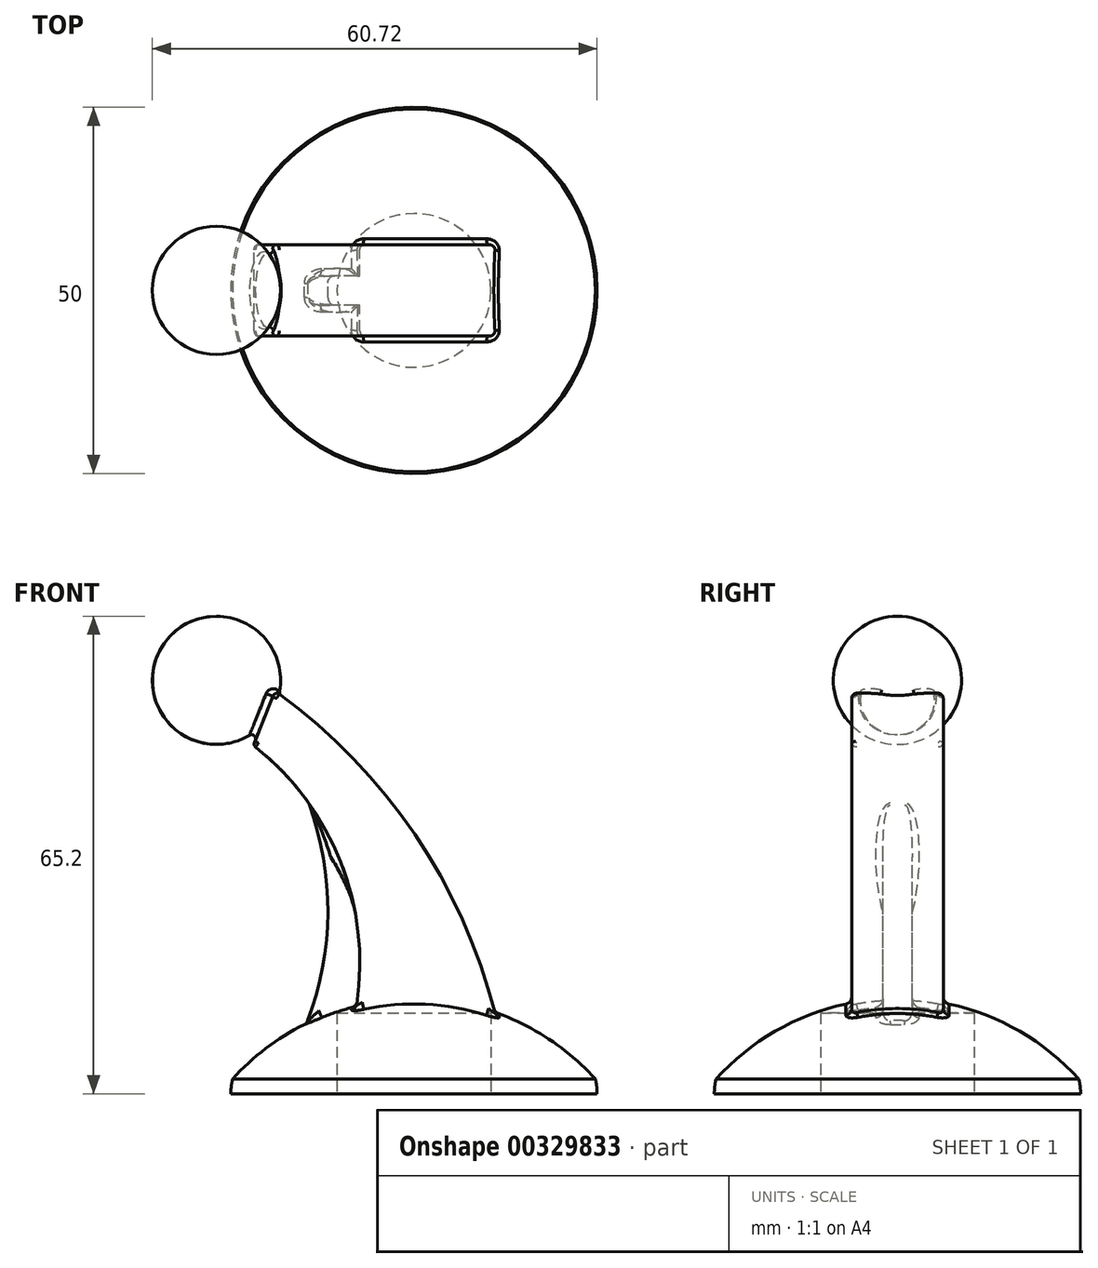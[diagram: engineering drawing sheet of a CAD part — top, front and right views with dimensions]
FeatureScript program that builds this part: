
annotation { "Feature Type Name" : "Feature", "Feature Type Description" : "" }
export const myFeature = defineFeature(function(context is Context, id is Id, definition is map)
    precondition{}
    {
        {
            assignVariable(context, id + "F0", {"name" : "magDepth", "anyValue" : 11});
        }
        {
            var Q0;
            Q0=qCreatedBy(makeId("Front.planeOp"),FACE);
            var sketch = newSketch(context, id + "F1", { "sketchPlane" : qUnion([Q0])});
            skLineSegment(sketch, "E0", {"start": v(0, 13) * mm, "end": v(0, 0) * mm});
            skLineSegment(sketch, "E1", {"start": v(0, 0) * mm, "end": v(25, 0) * mm});
            skArc(sketch, "E2", {"start": v(25, 0) * mm, "mid": v(24.94, 1) * mm, "end": v(24.77, 2) * mm});
            skArc(sketch, "E3", {"start": v(24.77, 2) * mm, "mid": v(13.55, 10.13) * mm, "end": v(0, 13) * mm});
            skLineSegment(sketch, "E4", {"start": v(0, 13) * mm, "end": v(-1.98, 13) * mm, "construction": true});
            skLineSegment(sketch, "E5", {"start": v(25, 0) * mm, "end": v(25, -2.25) * mm, "construction": true});
            skSolve(sketch);
        }
        {
            var Q0;
            Q0=makeQuery(id+"F1.imprint","IMPRINT",FACE,{"disambiguationData":[TD([[makeQuery(id+"F1.imprint","IMPRINT",EDGE,{"derivedFrom":sQuery(id+"F1.wireOp",EDGE,"E0")}),1.0]])]});
            var Q1;
            Q1=sQuery(id+"F1.wireOp",EDGE,"E0");
            revolve(context, id + "F2", {"entities" : qUnion([Q0]), "axis" : qUnion([Q1]), "revolveType" : RevolveType.FULL});
        }
        {
            var Q0;
            Q0=qCreatedBy(makeId("Front.planeOp"),FACE);
            var sketch = newSketch(context, id + "F3", { "sketchPlane" : qUnion([Q0])});
            skArc(sketch, "E6", {"start": v(13.03, 0) * mm, "mid": v(2.93, 30.93) * mm, "end": v(-18.97, 55) * mm});
            skArc(sketch, "E7", {"start": v(-11.84, 0) * mm, "mid": v(-8.2, 25.63) * mm, "end": v(-21.94, 47.57) * mm});
            skLineSegment(sketch, "E8", {"start": v(-21.94, 47.57) * mm, "end": v(-18.97, 55) * mm});
            skLineSegment(sketch, "E9", {"start": v(-11.84, 0) * mm, "end": v(13.03, 0) * mm});
            skSolve(sketch);
        }
        {
            var Q0;
            Q0 = qSketchRegion(id + "F3", true);
            extrude(context, id + "F4", {"entities" : qUnion([Q0]), "operationType" : NewBodyOperationType.ADD, "depth" : 12.5 * mm, "offsetDistance" : 25 * mm, "symmetric" : true});
        }
        {
            var Q0;
            Q0=qCreatedBy(makeId("Front.planeOp"),FACE);
            var sketch = newSketch(context, id + "F5", { "sketchPlane" : qUnion([Q0])});
            skArc(sketch, "E10", {"start": v(-7.92, 11.44) * mm, "mid": v(-8.33, 26.17) * mm, "end": v(-14.34, 39.62) * mm});
            skArc(sketch, "E11", {"start": v(-17.04, 4.49) * mm, "mid": v(-11.88, 21.76) * mm, "end": v(-14.34, 39.62) * mm});
            skLineSegment(sketch, "E12", {"start": v(-17.04, 4.49) * mm, "end": v(-7.92, 11.44) * mm});
            skSolve(sketch);
        }
        {
            var Q0;
            Q0 = qSketchRegion(id + "F5", true);
            extrude(context, id + "F6", {"entities" : qUnion([Q0]), "operationType" : NewBodyOperationType.ADD, "depth" : 4 * mm, "offsetDistance" : 25 * mm, "symmetric" : true});
        }
        {
            var Q0;
            Q0=qCreatedBy(makeId("Front.planeOp"),FACE);
            var sketch = newSketch(context, id + "F7", { "sketchPlane" : qUnion([Q0])});
            skArc(sketch, "E13", {"start": v(-26.97, 65.2) * mm, "mid": v(-35.72, 56.45) * mm, "end": v(-26.97, 47.7) * mm});
            skLineSegment(sketch, "E14", {"start": v(-26.97, 65.2) * mm, "end": v(-26.97, 47.7) * mm});
            skSolve(sketch);
        }
        {
            var Q0;
            Q0=makeQuery(id+"F7.imprint","IMPRINT",FACE,{"disambiguationData":[TD([[makeQuery(id+"F7.imprint","IMPRINT",EDGE,{"derivedFrom":sQuery(id+"F7.wireOp",EDGE,"E13")}),1.0]])]});
            var Q1;
            Q1=sQuery(id+"F7.wireOp",EDGE,"E14");
            revolve(context, id + "F8", {"operationType" : NewBodyOperationType.ADD, "entities" : qUnion([Q0]), "axis" : qUnion([Q1]), "revolveType" : RevolveType.FULL});
        }
        {
            var Q0;
            Q0=makeQuery(id+"F4.opExtrude","CAP_EDGE",EDGE,{"disambiguationData":[OSD([sQuery(id+"F3.wireOp",EDGE,"E8")])],"isStart":true});
            var Q1;
            Q1=makeQuery(id+"F4.opExtrude","CAP_EDGE",EDGE,{"disambiguationData":[OSD([sQuery(id+"F3.wireOp",EDGE,"E8")])],"isStart":false});
            var Q2;
            {var subQ0=sQuery(id+"F3.wireOp",EDGE,"E8");var subQ1=sQuery(id+"F3.wireOp",EDGE,"E7");Q2=makeQuery(id+"F8.boolean.opBoolean","SPLIT",EDGE,{"disambiguationData":[TD([makeQuery(id+"F4.opExtrude","CAP_FACE",FACE,{"disambiguationData":[OSD([sQuery(id+"F3.wireOp",EDGE,"E6"),subQ1,subQ0,sQuery(id+"F3.wireOp",EDGE,"E9")])],"isStart":false})])],"derivedFrom":makeQuery(id+"F4.opExtrude","SWEPT_EDGE",EDGE,{"disambiguationData":[OSD([subQ1,subQ0])]})});}
            var Q3;
            {var subQ0=sQuery(id+"F3.wireOp",EDGE,"E8");var subQ1=sQuery(id+"F3.wireOp",EDGE,"E7");Q3=makeQuery(id+"F8.boolean.opBoolean","SPLIT",EDGE,{"disambiguationData":[TD([makeQuery(id+"F4.opExtrude","CAP_FACE",FACE,{"disambiguationData":[OSD([sQuery(id+"F3.wireOp",EDGE,"E6"),subQ1,subQ0,sQuery(id+"F3.wireOp",EDGE,"E9")])],"isStart":true})])],"derivedFrom":makeQuery(id+"F4.opExtrude","SWEPT_EDGE",EDGE,{"disambiguationData":[OSD([subQ1,subQ0])]})});}
            var Q4;
            {var subQ0=sQuery(id+"F3.wireOp",EDGE,"E6");var subQ1=sQuery(id+"F3.wireOp",EDGE,"E8");Q4=makeQuery(id+"F8.boolean.opBoolean","SPLIT",EDGE,{"disambiguationData":[TD([makeQuery(id+"F4.opExtrude","CAP_FACE",FACE,{"disambiguationData":[OSD([subQ0,sQuery(id+"F3.wireOp",EDGE,"E7"),subQ1,sQuery(id+"F3.wireOp",EDGE,"E9")])],"isStart":false})])],"derivedFrom":makeQuery(id+"F4.opExtrude","SWEPT_EDGE",EDGE,{"disambiguationData":[OSD([subQ0,subQ1])]})});}
            var Q5;
            {var subQ0=sQuery(id+"F3.wireOp",EDGE,"E6");var subQ1=sQuery(id+"F3.wireOp",EDGE,"E8");Q5=makeQuery(id+"F8.boolean.opBoolean","SPLIT",EDGE,{"disambiguationData":[TD([makeQuery(id+"F4.opExtrude","CAP_FACE",FACE,{"disambiguationData":[OSD([subQ0,sQuery(id+"F3.wireOp",EDGE,"E7"),subQ1,sQuery(id+"F3.wireOp",EDGE,"E9")])],"isStart":true})])],"derivedFrom":makeQuery(id+"F4.opExtrude","SWEPT_EDGE",EDGE,{"disambiguationData":[OSD([subQ0,subQ1])]})});}
            var Q6;
            Q6=makeQuery(id+"F8.boolean.opBoolean","INTERSECT",EDGE,{"derivedFrom":[makeQuery(id+"F4.opExtrude","SWEPT_FACE",FACE,{"disambiguationData":[OSD([sQuery(id+"F3.wireOp",EDGE,"E6")])]}),makeQuery(id+"F8.opRevolve","SWEPT_FACE",FACE,{"disambiguationData":[OSD([sQuery(id+"F7.wireOp",EDGE,"E13")])]})]});
            var Q7;
            Q7=makeQuery(id+"F8.boolean.opBoolean","INTERSECT",EDGE,{"derivedFrom":[makeQuery(id+"F4.opExtrude","SWEPT_FACE",FACE,{"disambiguationData":[OSD([sQuery(id+"F3.wireOp",EDGE,"E7")])]}),makeQuery(id+"F8.opRevolve","SWEPT_FACE",FACE,{"disambiguationData":[OSD([sQuery(id+"F7.wireOp",EDGE,"E13")])]})]});
            var Q8;
            Q8=makeQuery(id+"F8.boolean.opBoolean","INTERSECT",EDGE,{"disambiguationData":[OD(0.0)],"derivedFrom":[makeQuery(id+"F4.opExtrude","SWEPT_FACE",FACE,{"disambiguationData":[OSD([sQuery(id+"F3.wireOp",EDGE,"E8")])]}),makeQuery(id+"F8.opRevolve","SWEPT_FACE",FACE,{"disambiguationData":[OSD([sQuery(id+"F7.wireOp",EDGE,"E13")])]})]});
            fillet(context, id + "F9", {"entities" : qUnion([Q0, Q1, Q2, Q3, Q4, Q5, Q6, Q7, Q8]), "radius" : .55 * mm, "tangentPropagation" : true, "allowEdgeOverflow" : false});
        }
        {
            var Q0;
            Q0=makeQuery(id+"F4.opExtrude","CAP_EDGE",EDGE,{"disambiguationData":[OSD([sQuery(id+"F3.wireOp",EDGE,"E7")])],"isStart":false});
            var Q1;
            Q1=makeQuery(id+"F4.opExtrude","CAP_EDGE",EDGE,{"disambiguationData":[OSD([sQuery(id+"F3.wireOp",EDGE,"E6")])],"isStart":false});
            var Q2;
            Q2=makeQuery(id+"F4.opExtrude","CAP_EDGE",EDGE,{"disambiguationData":[OSD([sQuery(id+"F3.wireOp",EDGE,"E7")])],"isStart":true});
            var Q3;
            Q3=makeQuery(id+"F4.opExtrude","CAP_EDGE",EDGE,{"disambiguationData":[OSD([sQuery(id+"F3.wireOp",EDGE,"E6")])],"isStart":true});
            fillet(context, id + "F10", {"entities" : qUnion([Q0, Q1, Q2, Q3]), "radius" : .7 * mm, "tangentPropagation" : true, "allowEdgeOverflow" : false});
        }
        {
            var Q0;
            Q0=makeQuery(id+"F6.opExtrude","CAP_EDGE",EDGE,{"disambiguationData":[OSD([sQuery(id+"F5.wireOp",EDGE,"E11")])],"isStart":false});
            var Q1;
            Q1=makeQuery(id+"F6.opExtrude","SWEPT_FACE",FACE,{"disambiguationData":[OSD([sQuery(id+"F5.wireOp",EDGE,"E11")])]});
            var Q2;
            Q2=makeQuery(id+"F6.boolean.opBoolean","INTERSECT",EDGE,{"derivedFrom":[makeQuery(id+"F2.opRevolve","SWEPT_FACE",FACE,{"disambiguationData":[OSD([sQuery(id+"F1.wireOp",EDGE,"E3")])]}),makeQuery(id+"F6.opExtrude","SWEPT_FACE",FACE,{"disambiguationData":[OSD([sQuery(id+"F5.wireOp",EDGE,"E11")])]})]});
            var Q3;
            Q3=makeQuery(id+"F4.boolean.opBoolean","INTERSECT",EDGE,{"derivedFrom":[makeQuery(id+"F2.opRevolve","SWEPT_FACE",FACE,{"disambiguationData":[OSD([sQuery(id+"F1.wireOp",EDGE,"E3")])]}),makeQuery(id+"F4.opExtrude","CAP_FACE",FACE,{"disambiguationData":[OSD([sQuery(id+"F3.wireOp",EDGE,"E6"),sQuery(id+"F3.wireOp",EDGE,"E7"),sQuery(id+"F3.wireOp",EDGE,"E8"),sQuery(id+"F3.wireOp",EDGE,"E9")])],"isStart":false})]});
            var Q4;
            Q4=makeQuery(id+"F10.opFillet","BLEND_EDGE",EDGE,{"blendedFrom":[makeQuery(id+"F4.opExtrude","CAP_EDGE",EDGE,{"disambiguationData":[OSD([sQuery(id+"F3.wireOp",EDGE,"E7")])],"isStart":false}),makeQuery(id+"F2.opRevolve","SWEPT_FACE",FACE,{"disambiguationData":[OSD([sQuery(id+"F1.wireOp",EDGE,"E3")])]})],"blendedInto":[makeQuery(id+"F2.opRevolve","SWEPT_FACE",FACE,{"disambiguationData":[OSD([sQuery(id+"F1.wireOp",EDGE,"E3")])]})]});
            var Q5;
            Q5=makeQuery(id+"F10.opFillet","BLEND_EDGE",EDGE,{"blendedFrom":[makeQuery(id+"F4.opExtrude","CAP_EDGE",EDGE,{"disambiguationData":[OSD([sQuery(id+"F3.wireOp",EDGE,"E6")])],"isStart":false}),makeQuery(id+"F2.opRevolve","SWEPT_FACE",FACE,{"disambiguationData":[OSD([sQuery(id+"F1.wireOp",EDGE,"E3")])]})],"blendedInto":[makeQuery(id+"F2.opRevolve","SWEPT_FACE",FACE,{"disambiguationData":[OSD([sQuery(id+"F1.wireOp",EDGE,"E3")])]})]});
            var Q6;
            Q6=makeQuery(id+"F4.boolean.opBoolean","INTERSECT",EDGE,{"derivedFrom":[makeQuery(id+"F2.opRevolve","SWEPT_FACE",FACE,{"disambiguationData":[OSD([sQuery(id+"F1.wireOp",EDGE,"E3")])]}),makeQuery(id+"F4.opExtrude","SWEPT_FACE",FACE,{"disambiguationData":[OSD([sQuery(id+"F3.wireOp",EDGE,"E6")])]})]});
            var Q7;
            Q7=makeQuery(id+"F10.opFillet","BLEND_EDGE",EDGE,{"blendedFrom":[makeQuery(id+"F4.opExtrude","CAP_EDGE",EDGE,{"disambiguationData":[OSD([sQuery(id+"F3.wireOp",EDGE,"E6")])],"isStart":true}),makeQuery(id+"F2.opRevolve","SWEPT_FACE",FACE,{"disambiguationData":[OSD([sQuery(id+"F1.wireOp",EDGE,"E3")])]})],"blendedInto":[makeQuery(id+"F2.opRevolve","SWEPT_FACE",FACE,{"disambiguationData":[OSD([sQuery(id+"F1.wireOp",EDGE,"E3")])]})]});
            var Q8;
            Q8=makeQuery(id+"F4.boolean.opBoolean","INTERSECT",EDGE,{"derivedFrom":[makeQuery(id+"F2.opRevolve","SWEPT_FACE",FACE,{"disambiguationData":[OSD([sQuery(id+"F1.wireOp",EDGE,"E3")])]}),makeQuery(id+"F4.opExtrude","CAP_FACE",FACE,{"disambiguationData":[OSD([sQuery(id+"F3.wireOp",EDGE,"E6"),sQuery(id+"F3.wireOp",EDGE,"E7"),sQuery(id+"F3.wireOp",EDGE,"E8"),sQuery(id+"F3.wireOp",EDGE,"E9")])],"isStart":true})]});
            var Q9;
            Q9=makeQuery(id+"F10.opFillet","BLEND_EDGE",EDGE,{"blendedFrom":[makeQuery(id+"F4.opExtrude","CAP_EDGE",EDGE,{"disambiguationData":[OSD([sQuery(id+"F3.wireOp",EDGE,"E7")])],"isStart":true}),makeQuery(id+"F2.opRevolve","SWEPT_FACE",FACE,{"disambiguationData":[OSD([sQuery(id+"F1.wireOp",EDGE,"E3")])]})],"blendedInto":[makeQuery(id+"F2.opRevolve","SWEPT_FACE",FACE,{"disambiguationData":[OSD([sQuery(id+"F1.wireOp",EDGE,"E3")])]})]});
            var Q10;
            {var subQ0=makeQuery(id+"F2.opRevolve","SWEPT_FACE",FACE,{"disambiguationData":[OSD([sQuery(id+"F1.wireOp",EDGE,"E3")])]});var subQ1=sQuery(id+"F3.wireOp",EDGE,"E7");var subQ2=makeQuery(id+"F4.opExtrude","SWEPT_FACE",FACE,{"disambiguationData":[OSD([subQ1])]});Q10=makeQuery(id+"F6.boolean.opBoolean","SPLIT",EDGE,{"disambiguationData":[TD([makeQuery(id+"F6.opExtrude","CAP_FACE",FACE,{"disambiguationData":[OSD([sQuery(id+"F5.wireOp",EDGE,"E10"),sQuery(id+"F5.wireOp",EDGE,"E11"),sQuery(id+"F5.wireOp",EDGE,"E12")])],"isStart":true})])],"derivedFrom":makeQuery(id+"F4.boolean.opBoolean","INTERSECT",EDGE,{"derivedFrom":[subQ0,subQ2]})});}
            var Q11;
            Q11=makeQuery(id+"F6.boolean.opBoolean","INTERSECT",EDGE,{"derivedFrom":[makeQuery(id+"F2.opRevolve","SWEPT_FACE",FACE,{"disambiguationData":[OSD([sQuery(id+"F1.wireOp",EDGE,"E3")])]}),makeQuery(id+"F6.opExtrude","CAP_FACE",FACE,{"disambiguationData":[OSD([sQuery(id+"F5.wireOp",EDGE,"E10"),sQuery(id+"F5.wireOp",EDGE,"E11"),sQuery(id+"F5.wireOp",EDGE,"E12")])],"isStart":true})]});
            var Q12;
            Q12=makeQuery(id+"F6.boolean.opBoolean","INTERSECT",EDGE,{"derivedFrom":[makeQuery(id+"F2.opRevolve","SWEPT_FACE",FACE,{"disambiguationData":[OSD([sQuery(id+"F1.wireOp",EDGE,"E3")])]}),makeQuery(id+"F6.opExtrude","CAP_FACE",FACE,{"disambiguationData":[OSD([sQuery(id+"F5.wireOp",EDGE,"E10"),sQuery(id+"F5.wireOp",EDGE,"E11"),sQuery(id+"F5.wireOp",EDGE,"E12")])],"isStart":false})]});
            var Q13;
            {var subQ0=makeQuery(id+"F2.opRevolve","SWEPT_FACE",FACE,{"disambiguationData":[OSD([sQuery(id+"F1.wireOp",EDGE,"E3")])]});var subQ1=sQuery(id+"F3.wireOp",EDGE,"E7");var subQ2=makeQuery(id+"F4.opExtrude","SWEPT_FACE",FACE,{"disambiguationData":[OSD([subQ1])]});Q13=makeQuery(id+"F6.boolean.opBoolean","SPLIT",EDGE,{"disambiguationData":[TD([makeQuery(id+"F6.opExtrude","CAP_FACE",FACE,{"disambiguationData":[OSD([sQuery(id+"F5.wireOp",EDGE,"E10"),sQuery(id+"F5.wireOp",EDGE,"E11"),sQuery(id+"F5.wireOp",EDGE,"E12")])],"isStart":false})])],"derivedFrom":makeQuery(id+"F4.boolean.opBoolean","INTERSECT",EDGE,{"derivedFrom":[subQ0,subQ2]})});}
            var Q14;
            Q14=makeQuery(id+"F6.opExtrude","SWEPT_EDGE",EDGE,{"disambiguationData":[OSD([sQuery(id+"F5.wireOp",EDGE,"E10"),sQuery(id+"F5.wireOp",EDGE,"E11")])]});
            var Q15;
            Q15=makeQuery(id+"F6.opExtrude","CAP_EDGE",EDGE,{"disambiguationData":[OSD([sQuery(id+"F5.wireOp",EDGE,"E11")])],"isStart":true});
            fillet(context, id + "F11", {"entities" : qUnion([Q0, Q1, Q2, Q3, Q4, Q5, Q6, Q7, Q8, Q9, Q10, Q11, Q12, Q13, Q14, Q15]), "radius" : 1 * mm, "tangentPropagation" : true, "allowEdgeOverflow" : false});
        }
        {
            var Q0;
            Q0=makeQuery(id+"F2.opRevolve","SWEPT_FACE",FACE,{"disambiguationData":[OSD([sQuery(id+"F1.wireOp",EDGE,"E1")])]});
            var sketch = newSketch(context, id + "F12", { "sketchPlane" : qUnion([Q0])});
            skCircle(sketch, "E15", {"center": v(0, 0) * mm, "radius": 10.5 * mm});
            skSolve(sketch);
        }
        {
            var Q0;
            Q0 = qSketchRegion(id + "F12", true);
            extrude(context, id + "F13", {"entities" : qUnion([Q0]), "operationType" : NewBodyOperationType.REMOVE, "oppositeDirection" : true, "depth" : (getVariable(context, 'magDepth')) * mm, "offsetDistance" : 25 * mm});
        }
    });
